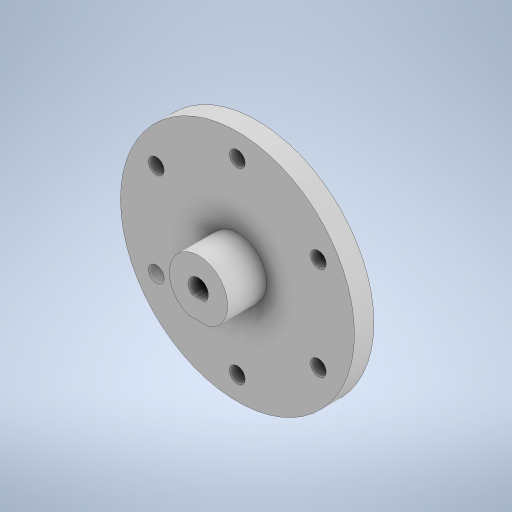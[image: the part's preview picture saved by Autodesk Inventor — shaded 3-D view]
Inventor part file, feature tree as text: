
AUTODESK INVENTOR PART (.ipt)
format: ipt  version: 2024 (Build 280153000, 153)  size: 324,096 bytes
history: native  units: mm
features: extrude x9, sketch x9
ambient origin geometry x8: Origin, YZ Plane, XZ Plane, XY Plane, X Axis, Y Axis, Z Axis, Center Point
bodies: Body1 (feature_tree)
feature tree (18):
  extrude  "Extrusion2"  Depth=5.0mm TaperAngle=0.0deg
  extrude  "Extrusion3"  Depth=7.0mm TaperAngle=0.0deg
  extrude  "Extrusion4"  Depth=10.0mm TaperAngle=0.0deg
  extrude  "Extrusion5"  Depth=4.5mm
  extrude  "Extrusion6"  Depth=2.0mm
  extrude  "Extrusion7"  Depth=20.0mm TaperAngle=0.0deg
  extrude  "Extrusion8"  Depth=15.0mm TaperAngle=0.0deg
  extrude  "Extrusion9"  Depth=24.0mm
  extrude  "Extrusion10"  Depth=20.0mm
  sketch  "Skizze2"  dims[d3=60.0mm d4=5.0mm d5=0.0mm]
  sketch  "Skizze3"  dims[d6=21.0mm d7=7.0mm d8=0.0mm]
  sketch  "Skizze4"  dims[d9=15.0mm d10=10.0mm d11=0.0mm]
  sketch  "Skizze5"  dims[d12=5.1mm d14=4.5mm]
  sketch  "Skizze6"  dims[d15=20.0mm d16=0.0mm d17=2.0mm]
  sketch  "Skizze7"  dims[d20=5.0mm d21=20.0mm d22=0.0mm]
  sketch  "Skizze8"  dims[d23=7.0mm d24=15.0mm d25=0.0mm]
  sketch  "Skizze9"  dims[d26=48.0mm d27=24.0mm]
  sketch  "Skizze11"  dims[d28=4.0mm d29=4.0mm d30=4.0mm d31=4.0mm d32=4.0mm d33=4.0mm d34=20.0mm d35=0.0mm d36=17.0mm d37=7.5mm d38=0.0mm d47=4.0mm d48=50.0mm d49=0.0mm d40=0.5mm d41=0.872665mm d42=0.5mm d43=0.872665mm]
